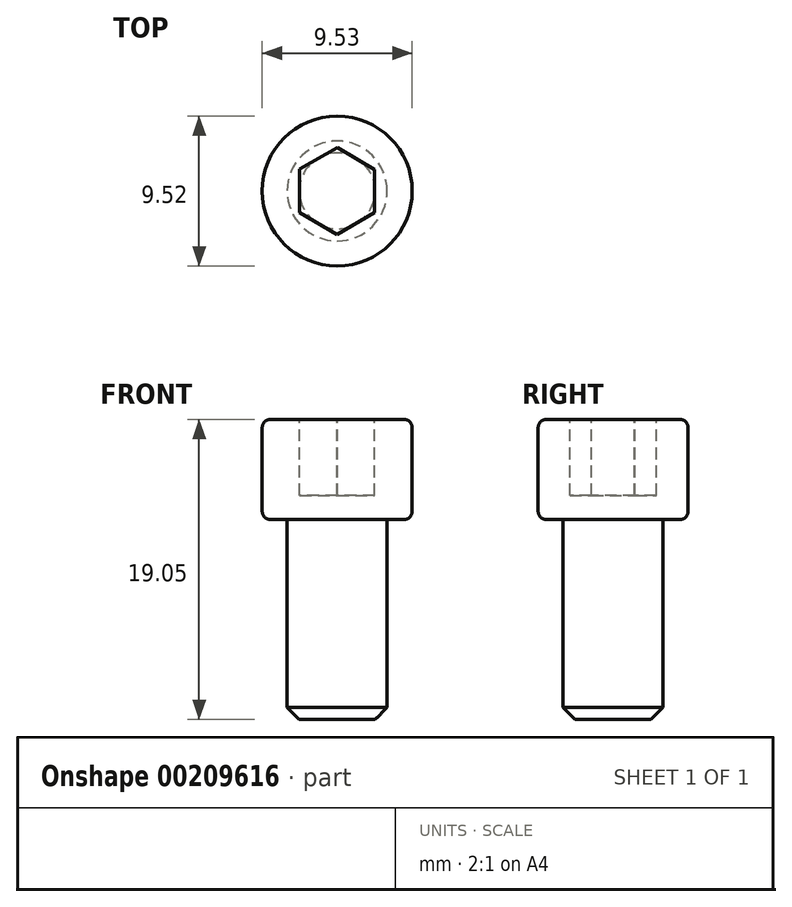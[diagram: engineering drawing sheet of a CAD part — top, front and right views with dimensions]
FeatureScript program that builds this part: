
annotation { "Feature Type Name" : "Feature", "Feature Type Description" : "" }
export const myFeature = defineFeature(function(context is Context, id is Id, definition is map)
    precondition{}
    {
        {
            var Q0;
            Q0=qCreatedBy(makeId("Top.planeOp"),FACE);
            var sketch = newSketch(context, id + "F0", { "sketchPlane" : qUnion([Q0])});
            skCircle(sketch, "E0", {"center": v(-48.02, -37.12) * mm, "radius": 3.18 * mm});
            skSolve(sketch);
        }
        {
            var Q0;
            Q0=makeQuery(id+"F0.imprint","IMPRINT",FACE,{"disambiguationData":[TD([[makeQuery(id+"F0.imprint","IMPRINT",EDGE,{"derivedFrom":sQuery(id+"F0.wireOp",EDGE,"E0")}),1.0]])]});
            extrude(context, id + "F1", {"entities" : qUnion([Q0]), "oppositeDirection" : true, "depth" : 12.7 * mm});
        }
        {
            var Q0;
            Q0=qCreatedBy(makeId("Top.planeOp"),FACE);
            var sketch = newSketch(context, id + "F2", { "sketchPlane" : qUnion([Q0])});
            skCircle(sketch, "E1.0", {"center": v(-48.02, -37.12) * mm, "radius": 3.18 * mm});
            skCircle(sketch, "E2", {"center": v(-48.02, -37.12) * mm, "radius": 4.76 * mm});
            skSolve(sketch);
        }
        {
            var Q0;
            Q0=makeQuery(id+"F2.imprint","IMPRINT",FACE,{"disambiguationData":[TD([[makeQuery(id+"F2.imprint","IMPRINT",EDGE,{"derivedFrom":sQuery(id+"F2.wireOp",EDGE,"E1.0")}),1.0]])]});
            var Q1;
            Q1=makeQuery(id+"F2.imprint","IMPRINT",FACE,{"disambiguationData":[TD([[makeQuery(id+"F2.imprint","IMPRINT",EDGE,{"derivedFrom":sQuery(id+"F2.wireOp",EDGE,"E1.0")}),-1.0]])]});
            extrude(context, id + "F3", {"entities" : qUnion([Q0, Q1]), "operationType" : NewBodyOperationType.ADD, "depth" : 6.35 * mm});
        }
        {
            var Q0;
            Q0=makeQuery(id+"F3.opExtrude","CAP_FACE",FACE,{"disambiguationData":[OSD([sQuery(id+"F2.wireOp",EDGE,"E2")])],"isStart":false});
            var sketch = newSketch(context, id + "F4", { "sketchPlane" : qUnion([Q0])});
            skCircle(sketch, "E3.0", {"center": v(-48.02, -37.12) * mm, "radius": 4.76 * mm});
            skCircle(sketch, "E4.cCircle", {"center": v(-48.02, -37.12) * mm, "radius": 2.38 * mm, "construction": true});
            skLineSegment(sketch, "E4.0", {"start": v(-50.4, -35.74) * mm, "end": v(-48.02, -34.37) * mm});
            skLineSegment(sketch, "E4.1", {"start": v(-48.02, -34.37) * mm, "end": v(-45.64, -35.75) * mm});
            skLineSegment(sketch, "E4.2", {"start": v(-45.64, -35.75) * mm, "end": v(-45.65, -38.5) * mm});
            skLineSegment(sketch, "E4.3", {"start": v(-45.65, -38.5) * mm, "end": v(-48.03, -39.87) * mm});
            skLineSegment(sketch, "E4.4", {"start": v(-48.03, -39.87) * mm, "end": v(-50.4, -38.49) * mm});
            skLineSegment(sketch, "E4.5", {"start": v(-50.4, -38.49) * mm, "end": v(-50.4, -35.74) * mm});
            skPoint(sketch, "E4.0.midPoint", {"position": v(-49.2, -35.05) * mm});
            skSolve(sketch);
        }
        {
            var Q0;
            Q0=makeQuery(id+"F4.imprint","IMPRINT",FACE,{"disambiguationData":[TD([[makeQuery(id+"F4.imprint","IMPRINT",EDGE,{"derivedFrom":sQuery(id+"F4.wireOp",EDGE,"E4.0")}),-1.0]])]});
            extrude(context, id + "F5", {"entities" : qUnion([Q0]), "operationType" : NewBodyOperationType.REMOVE, "oppositeDirection" : true, "depth" : 4.83 * mm});
        }
        {
            var Q0;
            Q0=makeQuery(id+"F1.opExtrude","CAP_EDGE",EDGE,{"disambiguationData":[OSD([sQuery(id+"F0.wireOp",EDGE,"E0")])],"isStart":false});
            chamfer(context, id + "F6", {"entities" : qUnion([Q0]), "chamferType" : ChamferType.OFFSET_ANGLE, "width" : 0.76 * mm, "oppositeDirection" : false, "angle" : 45 * degree, "tangentPropagation" : true});
        }
        {
            var Q0;
            Q0=qCreatedBy(makeId("Top.planeOp"),FACE);
            cPlane(context, id + "F7", {"entities" : qUnion([Q0]), "cplaneType" : CPlaneType.OFFSET, "offset" : 2.54 * mm, "oppositeDirection" : true, "width" : 152.4 * mm, "height" : 152.4 * mm});
        }
        {
            var Q0;
            Q0=qCreatedBy(id+"F7.planeOp",FACE);
            var sketch = newSketch(context, id + "F8", { "sketchPlane" : qUnion([Q0])});
            skCircle(sketch, "E5.0", {"center": v(-48.02, -37.12) * mm, "radius": 2.41 * mm});
            skSolve(sketch);
        }
        {
            var Q0;
            Q0=makeQuery(id+"F8.imprint","IMPRINT",FACE,{"disambiguationData":[TD([[makeQuery(id+"F8.imprint","IMPRINT",EDGE,{"derivedFrom":sQuery(id+"F8.wireOp",EDGE,"E5.0")}),-1.0]])]});
            var Q1;
            Q1=sQuery(id+"F8.wireOp",EDGE,"E5.0");
            var Q2;
            Q2=makeQuery(id+"F6.opChamfer","BLEND_FACE",FACE,{"disambiguationData":[OSD([sQuery(id+"F0.wireOp",EDGE,"E0")])]});
            extrude(context, id + "F9", {"entities" : qUnion([Q0]), "bodyType" : ToolBodyType.SURFACE, "surfaceEntities" : qUnion([Q1]), "endBound" : BoundingType.UP_TO_SURFACE, "oppositeDirection" : true, "endBoundEntityFace" : qUnion([Q2]), "depth" : 25.4 * mm});
        }
        {
            var Q0;
            Q0=makeQuery(id+"F3.opExtrude","CAP_EDGE",EDGE,{"disambiguationData":[OSD([sQuery(id+"F2.wireOp",EDGE,"E2")])],"isStart":true});
            var Q1;
            Q1=makeQuery(id+"F3.opExtrude","CAP_EDGE",EDGE,{"disambiguationData":[OSD([sQuery(id+"F2.wireOp",EDGE,"E2")])],"isStart":false});
            fillet(context, id + "F10", {"entities" : qUnion([Q0, Q1]), "radius" : 0.5 * mm, "tangentPropagation" : true, "allowEdgeOverflow" : false});
        }
    });
